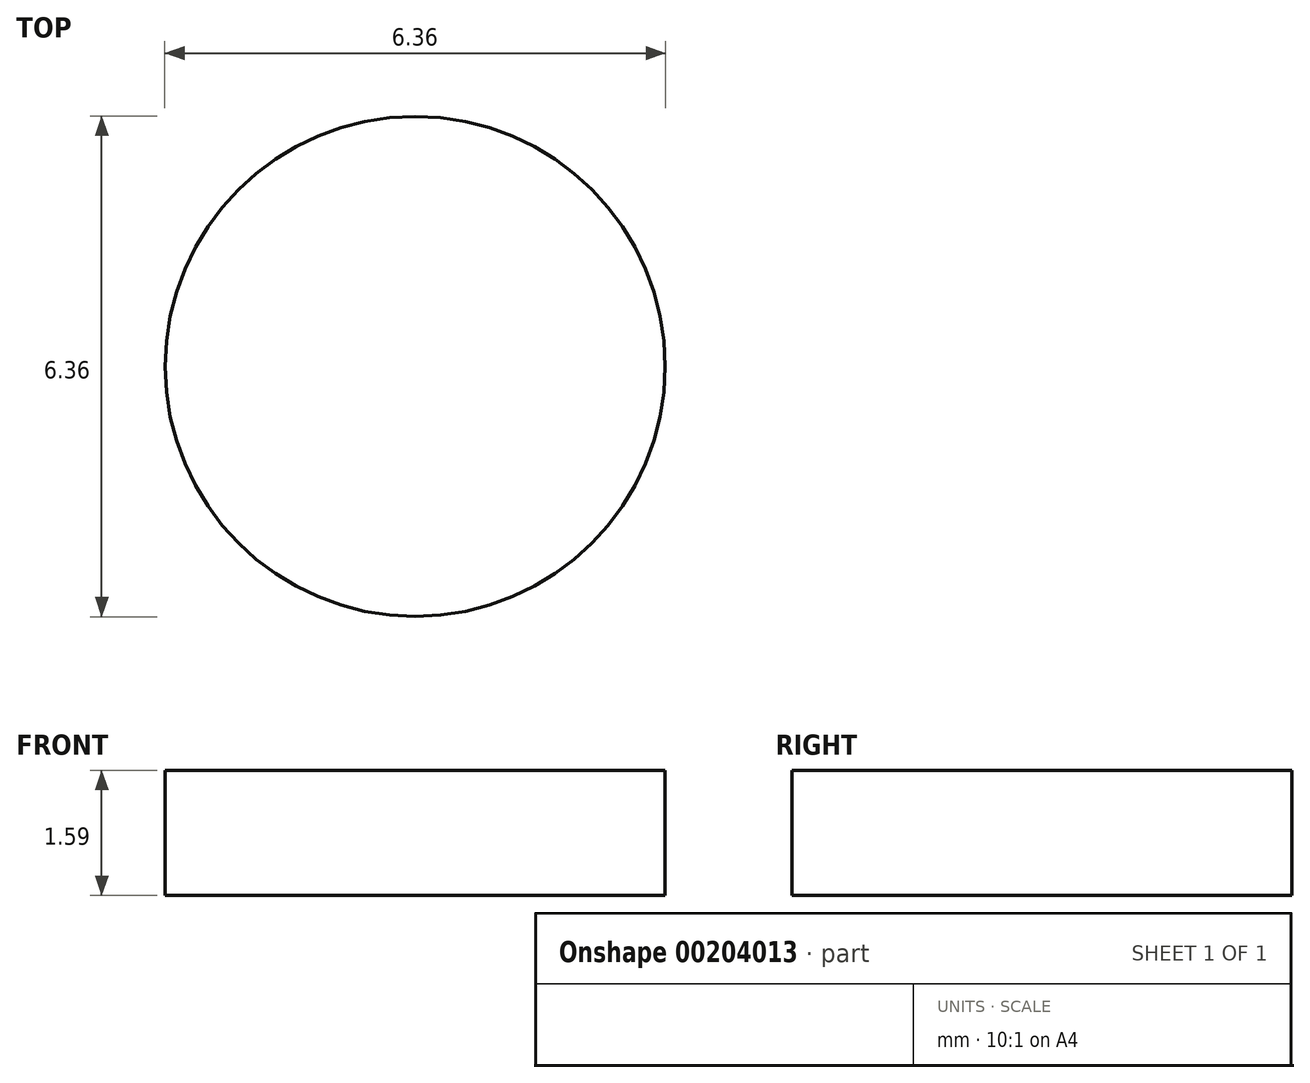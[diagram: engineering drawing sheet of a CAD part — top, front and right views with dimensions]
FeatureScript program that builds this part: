
annotation { "Feature Type Name" : "Feature", "Feature Type Description" : "" }
export const myFeature = defineFeature(function(context is Context, id is Id, definition is map)
    precondition{}
    {
        {
            var Q0;
            Q0=qCreatedBy(makeId("Top.planeOp"),FACE);
            var sketch = newSketch(context, id + "F0", { "sketchPlane" : qUnion([Q0])});
            skLineSegment(sketch, "E0.bottom", {"start": v(0, 0) * mm, "end": v(6.35, 0) * mm});
            skLineSegment(sketch, "E0.top", {"start": v(0, 6.35) * mm, "end": v(6.35, 6.35) * mm});
            skLineSegment(sketch, "E0.left", {"start": v(0, 0) * mm, "end": v(0, 6.35) * mm});
            skLineSegment(sketch, "E0.right", {"start": v(6.35, 0) * mm, "end": v(6.35, 6.35) * mm});
            skCircle(sketch, "E1", {"center": v(0, 0) * mm, "radius": 3.18 * mm});
            skSolve(sketch);
        }
        {
            var Q0;
            {var subQ0=sQuery(id+"F0.wireOp",EDGE,"E0.left");var subQ1=sQuery(id+"F0.wireOp",EDGE,"E0.bottom");var subQ2=makeQuery(id+"F0.imprint","INTERSECT",VERTEX,{"derivedFrom":[subQ1,subQ0]});Q0=makeQuery(id+"F0.imprint","IMPRINT",FACE,{"disambiguationData":[TD([[makeQuery(id+"F0.imprint","IMPRINT",EDGE,{"disambiguationData":[TD([[subQ2,-1.0]])],"derivedFrom":subQ1}),-1.0]])]});}
            var Q1;
            {var subQ0=sQuery(id+"F0.wireOp",EDGE,"E0.left");var subQ1=sQuery(id+"F0.wireOp",EDGE,"E0.bottom");var subQ2=makeQuery(id+"F0.imprint","INTERSECT",VERTEX,{"derivedFrom":[subQ1,subQ0]});Q1=makeQuery(id+"F0.imprint","IMPRINT",FACE,{"disambiguationData":[TD([[makeQuery(id+"F0.imprint","IMPRINT",EDGE,{"disambiguationData":[TD([[subQ2,-1.0]])],"derivedFrom":subQ1}),1.0]])]});}
            extrude(context, id + "F1", {"entities" : qUnion([Q0, Q1]), "depth" : 1.59 * mm});
        }
    });
